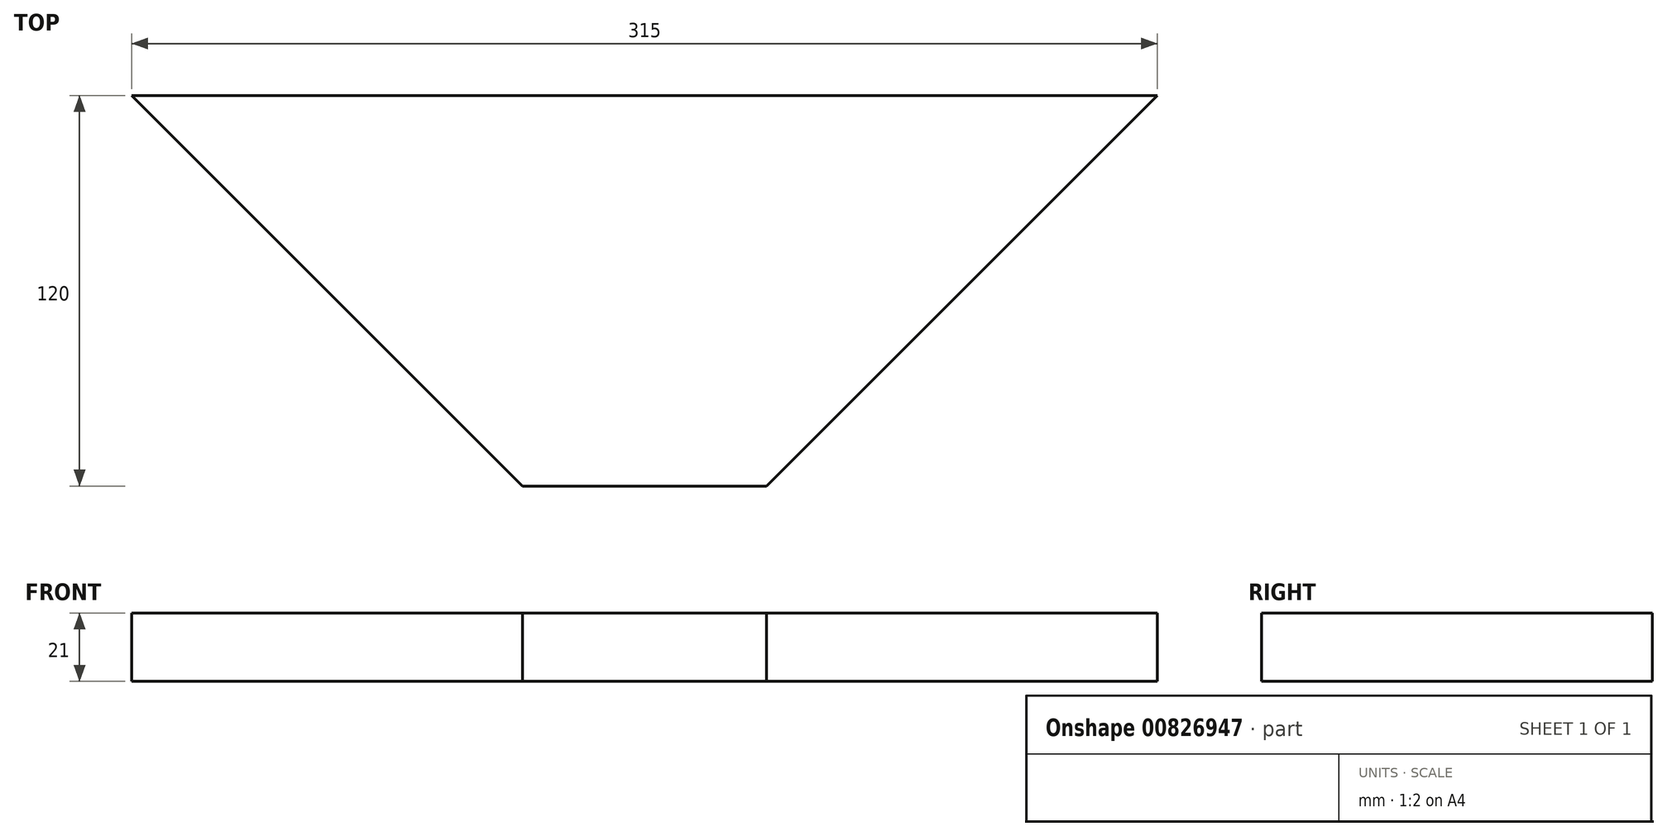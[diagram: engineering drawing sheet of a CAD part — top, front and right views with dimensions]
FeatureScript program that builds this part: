
annotation { "Feature Type Name" : "Feature", "Feature Type Description" : "" }
export const myFeature = defineFeature(function(context is Context, id is Id, definition is map)
    precondition{}
    {
        {
            var Q0;
            Q0=qCreatedBy(makeId("Top.planeOp"),FACE);
            var sketch = newSketch(context, id + "F0", { "sketchPlane" : qUnion([Q0])});
            skLineSegment(sketch, "E0", {"start": v(-37.5, -60) * mm, "end": v(37.5, -60) * mm});
            skLineSegment(sketch, "E1", {"start": v(37.5, -60) * mm, "end": v(157.5, 60) * mm});
            skLineSegment(sketch, "E2", {"start": v(157.5, 60) * mm, "end": v(-157.5, 60) * mm});
            skLineSegment(sketch, "E3", {"start": v(-157.5, 60) * mm, "end": v(-37.5, -60) * mm});
            skSolve(sketch);
        }
        {
            var Q0;
            Q0=qSketchRegion(id+"F0",true);
            extrude(context, id + "F1", {"entities" : qUnion([Q0]), "depth" : 21 * mm, "offsetDistance" : 25 * mm});
        }
    });
